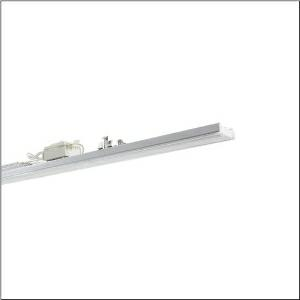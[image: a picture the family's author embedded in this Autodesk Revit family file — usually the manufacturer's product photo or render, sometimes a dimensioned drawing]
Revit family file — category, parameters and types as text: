
# Revit family: licross_11_recessed_ho_51te12dn4exm3s4
name_source: partatom
category: Lighting Fixtures
units: mm (PartAtom-declared; Revit-internal decimal feet)

## family parameters
Cut with Voids When Loaded = No
Host = Face
Light Source = No
Part Type = Normal
Room Calculation Point = No
Round Connector Dimension = Use Diameter
Shared = No

## types (1)
- --- (1 x LED, 1000 lm, 7.2 W, 4000K)
    Apparent Load = 7 VA
    CIE Flux Codes = 66 91 98 100 100
    Color Rendering = 80
    Color Temperature = 4000K
    Default Elevation = 1800 mm
    Description = Licross 11 Recessed HO, luminaire insert, of sheet steel, galvanised, coil coated, white, length: 1.500mm, width: 66mm, height: 67mm, LED rated luminous flux: 14.030lm, light colour: 840, SDCM (Standard Deviation of Colour Matching)MacAdam ≤ 2 SDCM (initial), control gear: DALI 2, with plug, 6-pole, with phase selection, for trunking rail, 9 or 11-core, mains connection: 220..240V, AC, 50/60Hz, rated input power: 81W, for trunking rail, 9-/11-core, internal wiring halogen-free, for emergency light function, converter,control gear: single battery element, battery: LiFePO4, 9Ah, primary optical cover: cover, of PMMA, light emission: direct distribution, primary light characteristic: symmetric, protection rating (complete): IP54, insulation class (complete): insulation class I (protective earthing), certification: CE, UKCA, protection symbol: D if used in an environment with non-conductive dust loads with corresponding accessories, impact resistance: IK06, permissible ambient temperature for indoor applications: +5..+30°C, standard: EN 60598-2-22, LABS conformity tested according to VDMA 24364:2018-05, reducing of maximum allowable ambient temperature of 5°C with ceiling mounting, corresponds to IFS (International Featured Standards) requirements for safety and quality in the food industry, The light source and the operating device comply with the requirements of the Ecodesign Regulation (EU) 2019/2020 and are replaceable in accordance with this regulation, packaging unit: 1 piece
    Height = 58 mm
    Lamp = 1 x LED
    Lamp Light Flux = 1000 lm
    Lamp Power = 7.2 W
    Lamp count = 1
    Length = 1500 mm
    Luminous efficacy = 139 lm/W
    Manufacturer = Siteco
    ModVariant = No
    Model = 51TE12DN4EXM3S4
    Mounting Place = Ceiling
    Mounting Type = Pendant
    Number of Poles = 1
    OnlyDefault = Yes
    Power Factor = 1
    Product Name = Licross 11 Recessed HO
    Product group = luminaire insert | ceiling pendant
    ProductGroupID = 901
    Protection Class = Protection class I
    Protection Degree = IP 54
    RLX_Detail_Level = 1
    RLX_Emergency_Light_Flux = 0 lm
    RLX_Emergency_Type = 0
    RLX_Emergency_Type_DB = No
    RlxData = <blob elided: 25265 chars, md5=4794fe78>
    Socket = socket
    Standby Power = 0 W
    System Light Flux = 1000 lm
    System Power = 7 W
    Type Comments = : emergency light operation: 3 h
    Type Image = l_1296930.jpg
    URL = http://relux.com
    VarID = @adj_093751
    Voltage = 0 V
    Weight = 0.00 kg
    Width = 66 mm

## geometry (parser evidence)
native form markers: Blend x4, Sweep x13
no freeform markers — native parametric forms only
